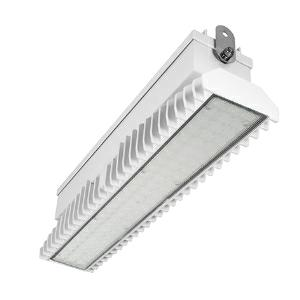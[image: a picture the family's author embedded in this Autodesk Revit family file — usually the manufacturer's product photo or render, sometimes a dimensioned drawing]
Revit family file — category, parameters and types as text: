
# Revit family: 3f_filippi_-_3f_lem_ho_ampio_3f_filippi_-_58953_a0812_-_3f_lem_1_ho_led_70_cr_ampio___vs_94c9
name_source: partatom
category: Lighting Fixtures
units: mm (PartAtom-declared; Revit-internal decimal feet)

## family parameters
Cut with Voids When Loaded = No
Host = Face
Light Source = No
Part Type = Normal
Room Calculation Point = No
Round Connector Dimension = Use Diameter
Shared = No

## types (1)
- 3F Filippi - 3F LEM HO Ampio (1 x LED, 8851 lm, 71 W, 4000 K)
    Apparent Load = 71 VA
    Approval mark = CE
    CIE Flux Codes = 67 90 97 100 100
    Color Rendering = 80
    Color Temperature = 4000 K
    Control Gear = Electronic ballast
    Default Elevation = 1800 mm
    Description = Industrial luminaire with high light output and high luminous efficiency designed with the most innovative technologies for environments with temperature up to 55°C.

ILLUMINOTECHNICAL
Luminous efficiency 100% (DLOR 98%, ULOR 2%).
Initial luminous flux of the luminaire 8851 lm.
Direct symmetric wide distribution: the illuminated area has a rectangular shape.
Installation Interdistance Transv.D = 1.24 x hu - Long.D = 1.20 x hu.
Tabular UGR (CIE 117 - 4H-8H; S=0.25H; 70/50/20): RUG 26.9 - 26.7.
Beam angle: 82° - 83°.
Luminous efficacy 125 lm/W.
Lifetime (L93/B10): 30000 h. (tq+25°C)
Lifetime (L90/B10): 50000 h. (tq+25°C)
Lifetime (L85/B10): 80000 h. (tq+25°C)
Lifetime (L80/B10): 100000 h. (tq+25°C)
Lifetime (L85/B10): 50000 h. (tq+55°C)
Sudden decreased luminous flux after 50000 hours: 0% (C0).
Photobiological safety in compliance with IEC/TR 62778: RG0 risk exempt, (IEC 62471).
In compliance with IEC/EN 62722-2-1 - IEC/EN 62717 standards.

SOURCE
Mid-Power linear LED module 70W/840.
Energy efficiency class (UE 2019/2020 - UE 2019/2015): C.
CIE 13.3 Colour rendering index: CRI >80 (R9 <50%).
IES TM-30 Fidelity Index: Rf = 84 Rg = 95.
CCT nominal colour temperature 4000 K.
Colour initial tolerance (MacAdam): SDCM 3.

MECHANICAL
Passive modular heatsinks in die-casted aluminium, painted in white colour.
To optimize the thermal management of the LED module, the heatsinks are oversized and provided with self-cleaning of cooling fins.
Wiring body in aluminium and galvanised steel anchored solidly to the sinks and thermally separated.
3F Lens lenses with high luminous efficiency, transparent methacrylate (PMMA), fixed to the LED modules.
Fixing brackets in stainless steel.
Luminaire with limited surface temperature. - D - (EN 60598-2-24)
Dimensions: 542x115 mm, height 154 mm. Weight 6.465 kg.
IP65 protection degree.
Mechanical strength to impacts IK06 (1 joule).
Glow-wire test resistance 650°C.

ELECTRICAL
Halogen Free electronic wiring 230V-50/60Hz, power factor 0.97, THD <25%, constant output current, class I, 1 driver.
Power of the luminaire 71 W.
ENEC - CE.
SAFE FLICKER: PstLM=<1 and SVM=<0.4 (IEC TR 61547-1 and IEC TR 63158), to ensure a more comfortable and safe light.
Luminaire compliant with EN 60598-2-22 for power supply from a centralised emergency system CPSS (Central Power Supply System), not incorporated in the luminaire - high risk areas excluded. The default power and flux are 100% in AC and 100% in DC.
Ambient temperature from -30°C to +55°C.
Temperature class T6 max 85°C.
Quick connection via M20 3P connector with 9-13 mm tightening range.
Power unit positioned on a separate compartment by the LED module to ensure optimum temperatures of cabling components, to be inspectable and maintainable.
Relative humidity UR: <85%.

INSTALLATION
Ceiling / Suspended / Wall.
All accessories dedicated to this product are available on the Catalog and on our website www.3F-Filippi.com.

ACCESSORIES
A0812 - Anti-glare microprismatic VS moulded glass, tempered, not flammable, with sealing gasket.
One required for each light module. The pack contains 10 pieces.

APPLICATIONS
In commercial environments, exhibition and industrial areas, stores, open areas.
Environments in which it is necessary a total protection against falling fragments (eg environments with foodstuffs or machines with moving parts or with extreme temperature changes), use luminaires with polycarbonate lenses.

WARNING
Fixture not suitable for cold stores with an ambient temperature <0°C and/or relative humidity >85%.
Luminaire designed for disposal/recycling at end-of-life.
Replaceable (LED only) light source by a professional. Replaceable control gear by a professional.
    Height = 154 mm
    Lamp = 1 x LED
    Lamp Light Flux = 8851 lm
    Lamp Power = 71 W
    Lamp count = 1
    Length = 542 mm
    Lifetime = 50000 h
    Luminous efficacy = 125 lm/W
    Manufacturer = 3F Filippi
    ModVariant = No
    Model = 3F Filippi - 58953+A0812 - 3F LEM 1 HO LED 70 CR AMPIO + VS
    Mounting Place = Ceiling
    Mounting Type = Pendant
    Number of Poles = 1
    OnlyDefault = Yes
    Power Factor = 1
    Product Name = 3F Filippi - 3F LEM HO Ampio
    Product group = pendant luminaire
    ProductGroupID = 9
    Protection Class = Protection class I
    Protection Degree = IP 65
    RLX_Detail_Level = 1
    RLX_Emergency_Light_Flux = 0 lm
    RLX_Emergency_Type = 0
    RLX_Emergency_Type_DB = No
    RlxData = <blob elided: 89909 chars, md5=17166de3>
    Socket = socket
    Standby Power = 0 W
    System Light Flux = 8851 lm
    System Power = 71 W
    Type Comments = Product without accessories
    Type Image = 3f_filippi_-_lem_1__a0812.jpg
    URL = http://relux.com
    VarID = ---
    Voltage = 0 V
    Weight = 0.00 kg
    Width = 115 mm

## geometry (parser evidence)
native form markers: Blend x4, Sweep x16
no freeform markers — native parametric forms only
